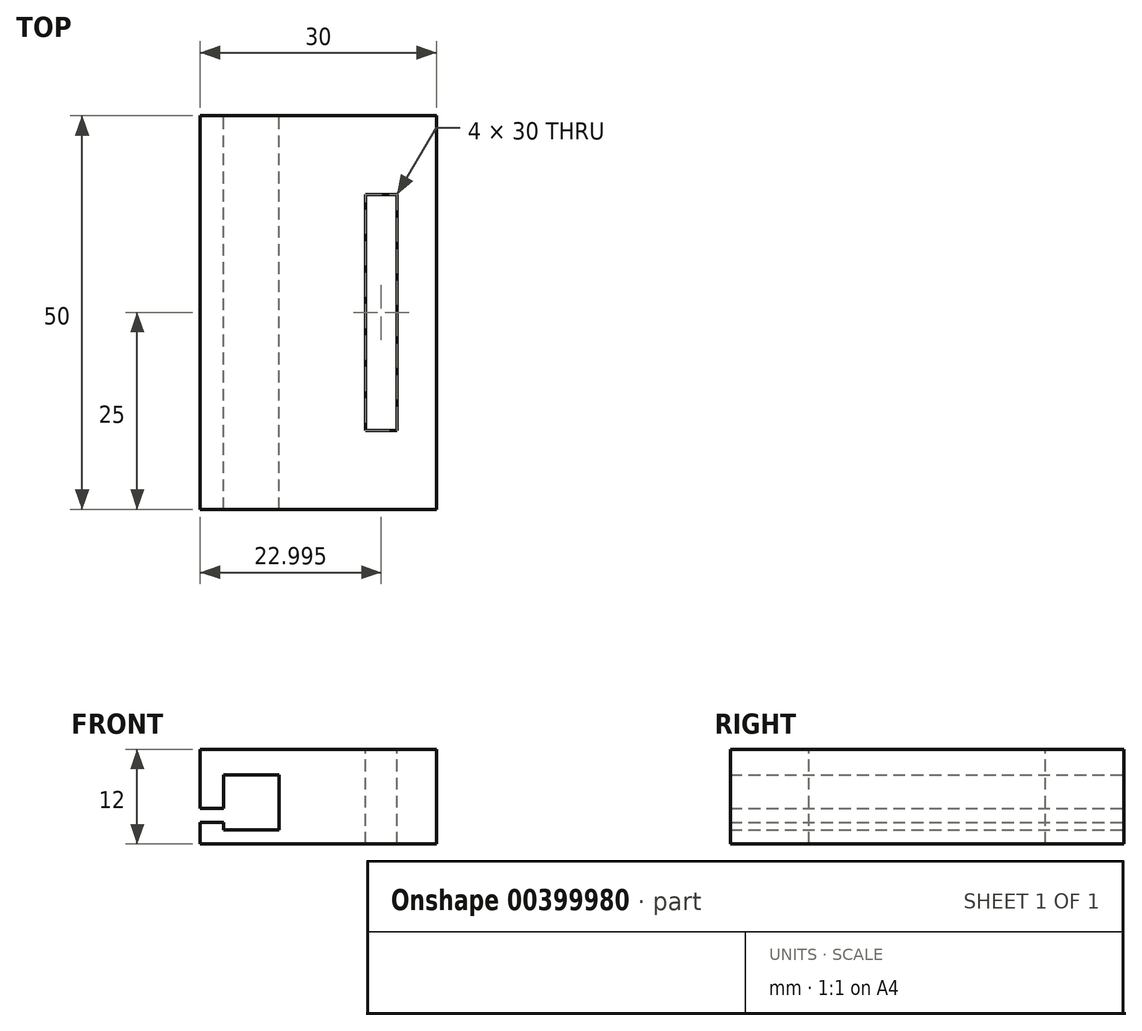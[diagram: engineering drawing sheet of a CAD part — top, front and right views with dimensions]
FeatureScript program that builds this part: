
annotation { "Feature Type Name" : "Feature", "Feature Type Description" : "" }
export const myFeature = defineFeature(function(context is Context, id is Id, definition is map)
    precondition{}
    {
        {
            var Q0;
            Q0=qCreatedBy(makeId("Front.planeOp"),FACE);
            var sketch = newSketch(context, id + "F0", { "sketchPlane" : qUnion([Q0])});
            skLineSegment(sketch, "E0", {"start": v(0, 0) * mm, "end": v(0, 51.25) * mm, "construction": true});
            skLineSegment(sketch, "E1", {"start": v(-40.62, 12) * mm, "end": v(-10.62, 12) * mm});
            skLineSegment(sketch, "E2", {"start": v(-40.62, 0) * mm, "end": v(-10.62, 0) * mm});
            skLineSegment(sketch, "E3", {"start": v(-40.62, 12) * mm, "end": v(-40.62, 4.5) * mm});
            skLineSegment(sketch, "E4", {"start": v(-40.62, 4.5) * mm, "end": v(-37.62, 4.5) * mm});
            skLineSegment(sketch, "E5", {"start": v(-37.62, 4.5) * mm, "end": v(-37.62, 8.75) * mm});
            skLineSegment(sketch, "E6", {"start": v(-37.62, 8.75) * mm, "end": v(-30.62, 8.75) * mm});
            skLineSegment(sketch, "E7", {"start": v(-30.62, 8.75) * mm, "end": v(-30.62, 1.75) * mm});
            skLineSegment(sketch, "E8", {"start": v(-30.62, 1.75) * mm, "end": v(-37.62, 1.75) * mm});
            skLineSegment(sketch, "E9", {"start": v(-37.62, 1.75) * mm, "end": v(-37.62, 2.7) * mm});
            skLineSegment(sketch, "E10", {"start": v(-37.62, 2.7) * mm, "end": v(-40.62, 2.7) * mm});
            skLineSegment(sketch, "E11", {"start": v(-40.62, 2.7) * mm, "end": v(-40.62, 0) * mm});
            skPoint(sketch, "E12.orphan", {"position": v(-32.7, 0) * mm});
            skLineSegment(sketch, "E13", {"start": v(-10.62, 12) * mm, "end": v(-10.62, 0) * mm});
            skPoint(sketch, "E14.end.orphan", {"position": v(22.06, 0) * mm});
            skSolve(sketch);
        }
        {
            var Q0;
            Q0 = qSketchRegion(id + "F0", true);
            extrude(context, id + "F1", {"entities" : qUnion([Q0]), "depth" : 50 * mm});
        }
        {
            var Q0;
            Q0=makeQuery(id+"F1.opExtrude","SWEPT_FACE",FACE,{"disambiguationData":[OSD([sQuery(id+"F0.wireOp",EDGE,"E1")])]});
            var sketch = newSketch(context, id + "F2", { "sketchPlane" : qUnion([Q0])});
            skLineSegment(sketch, "E15.bottom", {"start": v(-15.62, -40) * mm, "end": v(-19.62, -40) * mm});
            skLineSegment(sketch, "E15.top", {"start": v(-15.62, -10) * mm, "end": v(-19.62, -10) * mm});
            skLineSegment(sketch, "E15.left", {"start": v(-15.62, -40) * mm, "end": v(-15.62, -10) * mm});
            skLineSegment(sketch, "E15.right", {"start": v(-19.62, -40) * mm, "end": v(-19.62, -10) * mm});
            skSolve(sketch);
        }
        {
            var Q0;
            Q0 = qSketchRegion(id + "F2", true);
            extrude(context, id + "F3", {"entities" : qUnion([Q0]), "operationType" : NewBodyOperationType.REMOVE, "oppositeDirection" : true, "depth" : 25 * mm});
        }
    });
